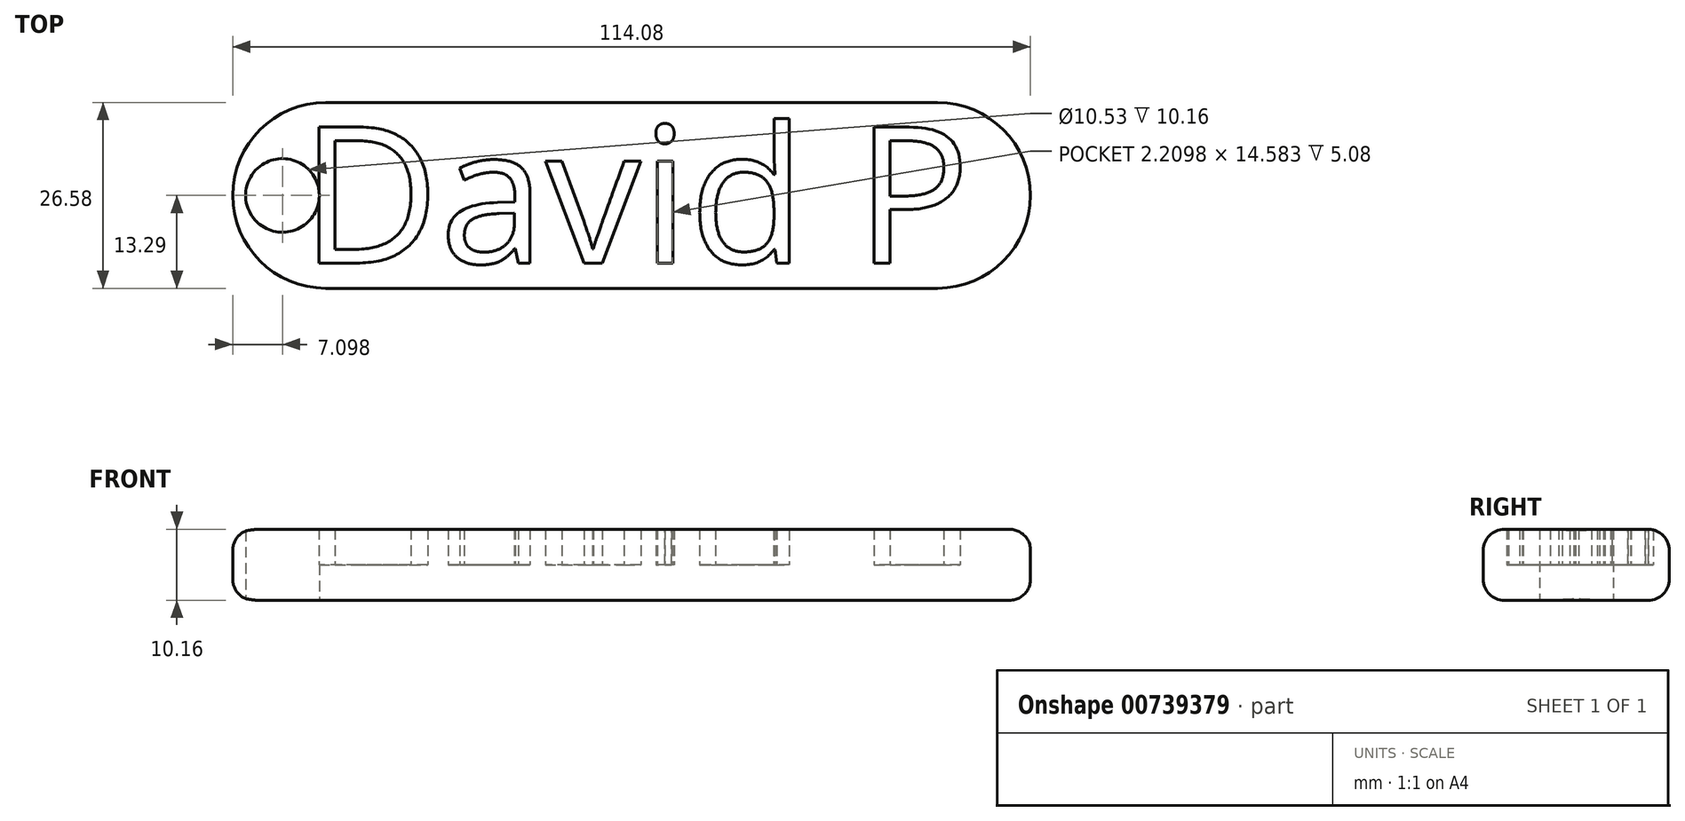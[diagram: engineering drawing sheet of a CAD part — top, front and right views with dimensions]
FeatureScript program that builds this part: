
annotation { "Feature Type Name" : "Feature", "Feature Type Description" : "" }
export const myFeature = defineFeature(function(context is Context, id is Id, definition is map)
    precondition{}
    {
        {
            var Q0;
            Q0=qCreatedBy(makeId("Top.planeOp"),FACE);
            var sketch = newSketch(context, id + "F0", { "sketchPlane" : qUnion([Q0])});
            skLineSegment(sketch, "E0", {"start": v(-43.75, 13.3) * mm, "end": v(0, 13.3) * mm});
            skLineSegment(sketch, "E1.MirrorCS", {"start": v(43.75, 13.3) * mm, "end": v(0, 13.3) * mm});
            skLineSegment(sketch, "E2.MirrorCS", {"start": v(-43.75, -13.3) * mm, "end": v(0, -13.3) * mm});
            skLineSegment(sketch, "E3.MirrorCS", {"start": v(43.75, -13.3) * mm, "end": v(0, -13.3) * mm});
            skArc(sketch, "E4", {"start": v(-43.75, 13.3) * mm, "mid": v(-57.04, 0) * mm, "end": v(-43.75, -13.3) * mm});
            skArc(sketch, "E5.MirrorCS", {"start": v(43.75, 13.3) * mm, "mid": v(57.04, 0) * mm, "end": v(43.75, -13.3) * mm});
            skCircle(sketch, "E6", {"center": v(-49.94, 0) * mm, "radius": 5.27 * mm});
            skSolve(sketch);
        }
        {
            var Q0;
            Q0 = qSketchRegion(id + "F0", true);
            extrude(context, id + "F1", {"entities" : qUnion([Q0]), "endBound" : BoundingType.SYMMETRIC, "depth" : 10.16 * mm, "offsetDistance" : 25.4 * mm});
        }
        {
            var Q0;
            Q0=qCreatedBy(makeId("Top.planeOp"),FACE);
            var sketch = newSketch(context, id + "F2", { "sketchPlane" : qUnion([Q0])});
            skText(sketch, "E7", { "text": "David P", "fontName": "OpenSans-Regular.ttf"});
            const initialGuessF2  = {"E7": [-0.04736, -0.00968, 1, 0, 0.01962]};
            skSetInitialGuess(sketch, initialGuessF2);
            skSolve(sketch);
        }
        {
            var Q0;
            Q0 = qSketchRegion(id + "F2", true);
            extrude(context, id + "F3", {"entities" : qUnion([Q0]), "operationType" : NewBodyOperationType.REMOVE, "depth" : 5.08 * mm, "offsetDistance" : 25.4 * mm});
        }
        {
            var Q0;
            Q0=makeQuery(id+"F1.opExtrude","CAP_EDGE",EDGE,{"disambiguationData":[OSD([sQuery(id+"F0.wireOp",EDGE,"E4")])],"isStart":false});
            var Q1;
            Q1=makeQuery(id+"F1.opExtrude","CAP_EDGE",EDGE,{"disambiguationData":[OSD([sQuery(id+"F0.wireOp",EDGE,"E4")])],"isStart":true});
            fillet(context, id + "F4", {"entities" : qUnion([Q0, Q1]), "radius" : 3 * mm, "tangentPropagation" : true, "allowEdgeOverflow" : false});
        }
    });
